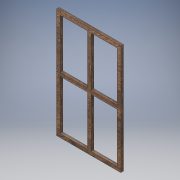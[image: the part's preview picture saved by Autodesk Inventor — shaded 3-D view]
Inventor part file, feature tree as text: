
AUTODESK INVENTOR PART (.ipt)
format: ipt  version: 2017 (Build 210142000, 142)  size: 137,216 bytes
history: native  units: in
note: dims shown in document units (in); Inventor stores cm internally (conversion verified against a paired STEP export)
features: extrude x2, sketch x2, projected_geometry x1
ambient origin geometry x8: Origin, YZ Plane, XZ Plane, XY Plane, X Axis, Y Axis, Z Axis, Center Point
bodies: Solid1 (feature_tree)
feature tree (5):
  extrude  "Extrusion1"  Depth=30.75in
  extrude  "Extrusion2"  Depth=0.75in TaperAngle=0.0deg
  sketch  "Sketch1"  dims[d0=18.0in d1=30.75in]
  sketch  "Sketch2"  dims[d2=0.75in d3=0.0in d22=0.75in d23=0.0in d24=1.0in d25=1.0in d26=1.0in d27=1.0in d28=1.0in d29=1.0in d30=1.0in d31=1.0in d32=1.0in d33=1.0in d34=7.3125in d35=7.6875in d36=13.875in]
  projected_geometry  "Projected Loop1"
